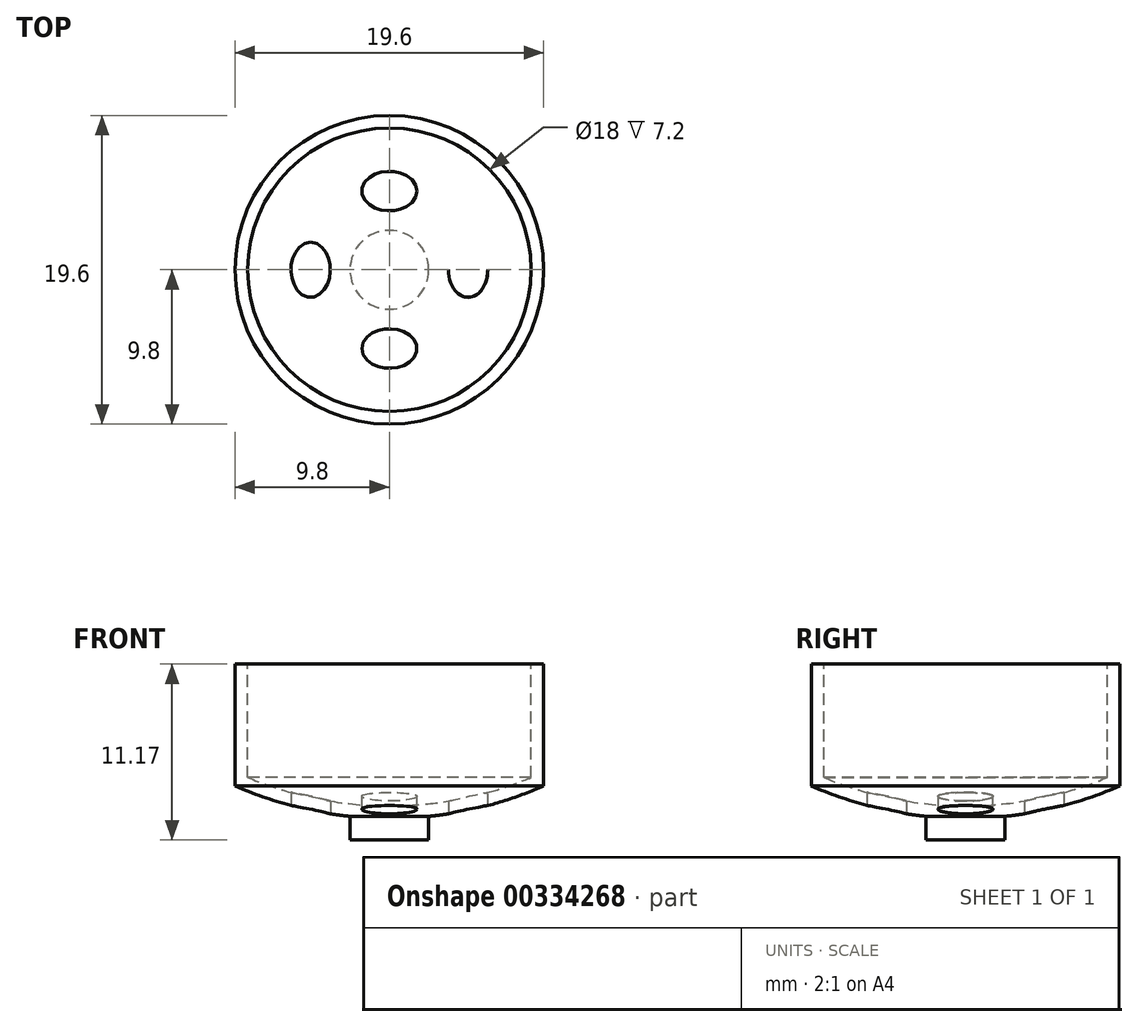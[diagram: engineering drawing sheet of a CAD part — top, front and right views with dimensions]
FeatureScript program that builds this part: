
annotation { "Feature Type Name" : "Feature", "Feature Type Description" : "" }
export const myFeature = defineFeature(function(context is Context, id is Id, definition is map)
    precondition{}
    {
        {
            var Q0;
            Q0=qCreatedBy(makeId("Front.planeOp"),FACE);
            var sketch = newSketch(context, id + "F0", { "sketchPlane" : qUnion([Q0])});
            skLineSegment(sketch, "E0", {"start": v(0, 0) * mm, "end": v(9, 0) * mm, "construction": true});
            skLineSegment(sketch, "E1", {"start": v(9, 0) * mm, "end": v(9, 7.2) * mm});
            skArc(sketch, "E2", {"start": v(-9, 0) * mm, "mid": v(-4.59, -1.35) * mm, "end": v(0, -1.8) * mm, "construction": true});
            skLineSegment(sketch, "E3", {"start": v(0, 21.6) * mm, "end": v(0, 0) * mm, "construction": true});
            skLineSegment(sketch, "E4", {"start": v(0, -1.8) * mm, "end": v(8.64, -1.8) * mm, "construction": true});
            skLineSegment(sketch, "E5", {"start": v(9, 7.2) * mm, "end": v(10.5, 7.2) * mm});
            skLineSegment(sketch, "E6", {"start": v(10.5, 7.2) * mm, "end": v(10.75, 15.2) * mm});
            skArc(sketch, "E7", {"start": v(0, -1.8) * mm, "mid": v(4.59, -1.35) * mm, "end": v(9, 0) * mm});
            skLineSegment(sketch, "E8.0", {"start": v(11.08, 0.08) * mm, "end": v(11.55, 15.2) * mm});
            skArc(sketch, "E8.3", {"start": v(0, -2.6) * mm, "mid": v(5.7, -1.92) * mm, "end": v(11.08, 0.08) * mm});
            skLineSegment(sketch, "E9", {"start": v(0, -1.8) * mm, "end": v(0, -2.6) * mm});
            skLineSegment(sketch, "E10", {"start": v(10.75, 15.2) * mm, "end": v(11.55, 15.2) * mm});
            skLineSegment(sketch, "E11", {"start": v(0, -2.6) * mm, "end": v(0, -3.97) * mm});
            skLineSegment(sketch, "E12", {"start": v(0, -3.97) * mm, "end": v(2.5, -3.97) * mm});
            skLineSegment(sketch, "E13", {"start": v(2.5, -3.97) * mm, "end": v(2.5, -2.47) * mm});
            skLineSegment(sketch, "E14", {"start": v(10.5, 7.2) * mm, "end": v(11.3, 7.2) * mm, "construction": true});
            skLineSegment(sketch, "E15", {"start": v(9.8, 7.2) * mm, "end": v(9.8, -0.53) * mm});
            skLineSegment(sketch, "E16", {"start": v(9, 5) * mm, "end": v(8.38, 3.34) * mm});
            skLineSegment(sketch, "E17", {"start": v(8.61, 3) * mm, "end": v(9, 3) * mm});
            skPoint(sketch, "E18.visualSharp", {"position": v(8.25, 3) * mm});
            skArc(sketch, "E18.filletArc", {"start": v(8.38, 3.34) * mm, "mid": v(8.4, 3.1) * mm, "end": v(8.61, 3) * mm});
            skSolve(sketch);
        }
        {
            var Q0;
            Q0=makeQuery(id+"F0.imprint","IMPRINT",FACE,{"disambiguationData":[TD([[makeQuery(id+"F0.imprint","IMPRINT",EDGE,{"derivedFrom":sQuery(id+"F0.wireOp",EDGE,"E1")}),-1.0]])]});
            var Q1;
            {var subQ0=sQuery(id+"F0.wireOp",EDGE,"E11");Q1=makeQuery(id+"F0.imprint","IMPRINT",FACE,{"disambiguationData":[TD([[makeQuery(id+"F0.imprint","IMPRINT",EDGE,{"derivedFrom":subQ0}),1.0]])]});}
            var Q2;
            Q2=sQuery(id+"F0.wireOp",EDGE,"E11");
            revolve(context, id + "F1", {"entities" : qUnion([Q0, Q1]), "axis" : qUnion([Q2]), "revolveType" : RevolveType.FULL});
        }
        {
            var Q0;
            Q0=qCreatedBy(makeId("Top.planeOp"),FACE);
            var sketch = newSketch(context, id + "F2", { "sketchPlane" : qUnion([Q0])});
            skCircle(sketch, "E19", {"center": v(0, 0) * mm, "radius": 5 * mm, "construction": true});
            skEllipse(sketch, "E20", {"center": v(0, -5) * mm, "majorRadius": 1.25 * mm, "minorRadius": 1.75 * mm, "majorAxis": v(0, 1)});
            skEllipse(sketch, "E21.1.0", {"center": v(5, 0) * mm, "majorRadius": 1.25 * mm, "minorRadius": 1.75 * mm, "majorAxis": v(-1, 0)});
            skEllipse(sketch, "E21.2.0", {"center": v(0, 5) * mm, "majorRadius": 1.25 * mm, "minorRadius": 1.75 * mm, "majorAxis": v(0, -1)});
            skEllipse(sketch, "E21.3.0", {"center": v(-5, 0) * mm, "majorRadius": 1.25 * mm, "minorRadius": 1.75 * mm, "majorAxis": v(1, 0)});
            skSolve(sketch);
        }
        {
            var Q0;
            Q0 = qSketchRegion(id + "F2", true);
            extrude(context, id + "F3", {"entities" : qUnion([Q0]), "operationType" : NewBodyOperationType.REMOVE, "oppositeDirection" : true, "depth" : 25 * mm});
        }
        {
            var Q0;
            Q0=qCreatedBy(makeId("Right.planeOp"),FACE);
            var sketch = newSketch(context, id + "F4", { "sketchPlane" : qUnion([Q0])});
            skLineSegment(sketch, "E22.bottom", {"start": v(2.5, 12.2) * mm, "end": v(-2.5, 12.2) * mm});
            skLineSegment(sketch, "E22.top", {"start": v(2.5, 9.7) * mm, "end": v(-2.5, 9.7) * mm});
            skLineSegment(sketch, "E22.left", {"start": v(3.5, 11.2) * mm, "end": v(3.5, 10.7) * mm});
            skLineSegment(sketch, "E22.right", {"start": v(-3.5, 11.2) * mm, "end": v(-3.5, 10.7) * mm});
            skLineSegment(sketch, "E23", {"start": v(0, 9.7) * mm, "end": v(0, 0) * mm, "construction": true});
            skPoint(sketch, "E24.visualSharp", {"position": v(3.5, 12.2) * mm});
            skArc(sketch, "E24.filletArc", {"start": v(3.5, 11.2) * mm, "mid": v(3.2, 11.9) * mm, "end": v(2.5, 12.2) * mm});
            skPoint(sketch, "E25.visualSharp", {"position": v(3.5, 9.7) * mm});
            skArc(sketch, "E25.filletArc", {"start": v(2.5, 9.7) * mm, "mid": v(3.2, 10) * mm, "end": v(3.5, 10.7) * mm});
            skPoint(sketch, "E26.visualSharp", {"position": v(-3.5, 9.7) * mm});
            skArc(sketch, "E26.filletArc", {"start": v(-3.5, 10.7) * mm, "mid": v(-3.2, 10) * mm, "end": v(-2.5, 9.7) * mm});
            skPoint(sketch, "E27.visualSharp", {"position": v(-3.5, 12.2) * mm});
            skArc(sketch, "E27.filletArc", {"start": v(-2.5, 12.2) * mm, "mid": v(-3.2, 11.9) * mm, "end": v(-3.5, 11.2) * mm});
            skSolve(sketch);
        }
        {
            var Q0;
            Q0 = qSketchRegion(id + "F4", true);
            extrude(context, id + "F5", {"entities" : qUnion([Q0]), "operationType" : NewBodyOperationType.REMOVE, "oppositeDirection" : true, "depth" : 25 * mm, "hasSecondDirection" : true, "secondDirectionOppositeDirection" : false, "secondDirectionDepth" : 25 * mm});
        }
    });
